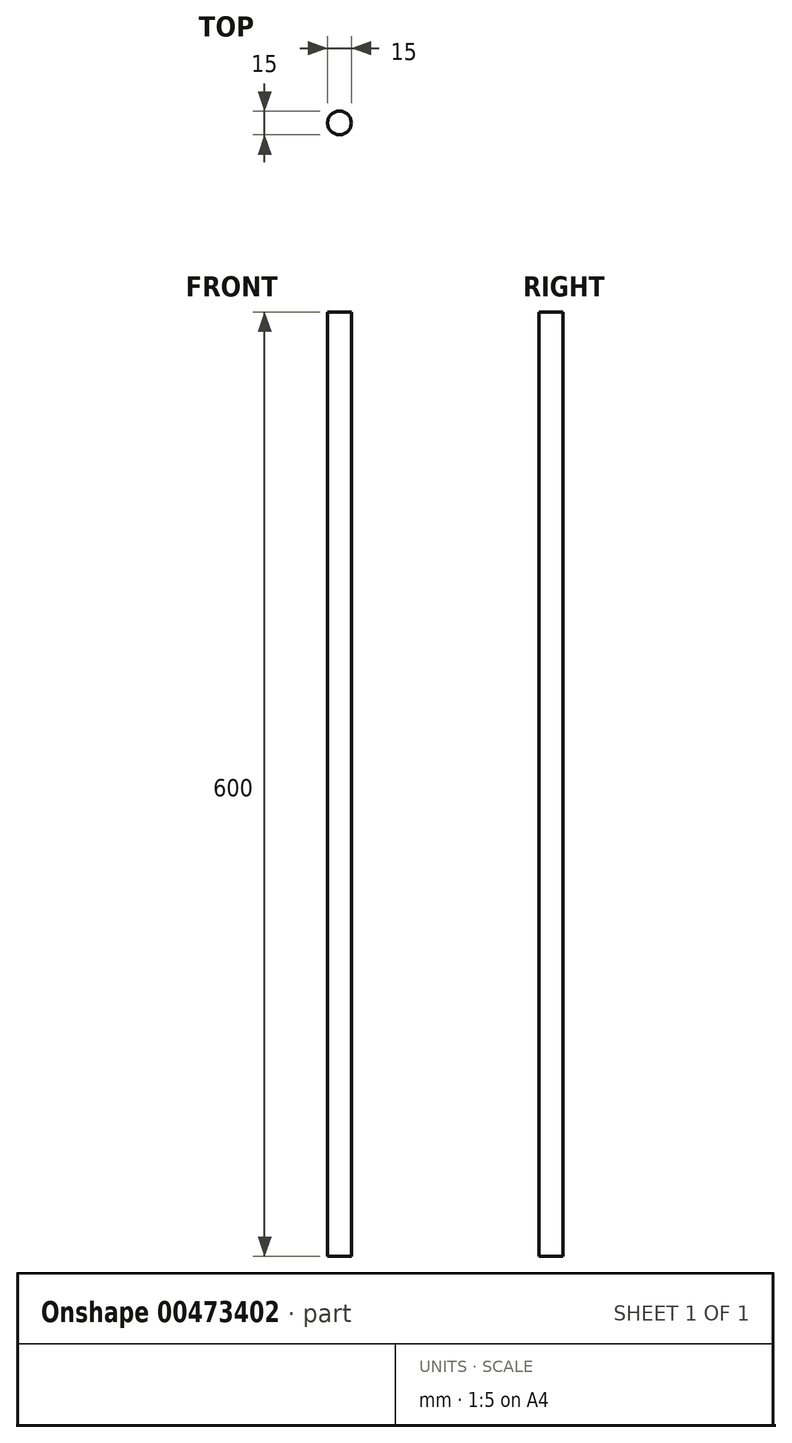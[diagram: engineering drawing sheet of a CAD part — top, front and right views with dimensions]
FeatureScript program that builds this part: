
annotation { "Feature Type Name" : "Feature", "Feature Type Description" : "" }
export const myFeature = defineFeature(function(context is Context, id is Id, definition is map)
    precondition{}
    {
        {
            var Q0;
            Q0=qCreatedBy(makeId("Top.planeOp"),FACE);
            var sketch = newSketch(context, id + "F0", { "sketchPlane" : qUnion([Q0])});
            skCircle(sketch, "E0", {"center": v(0, 0) * mm, "radius": 7.5 * mm});
            skSolve(sketch);
        }
        {
            var Q0;
            Q0 = qSketchRegion(id + "F0", true);
            extrude(context, id + "F1", {"entities" : qUnion([Q0]), "depth" : 600 * mm});
        }
    });
